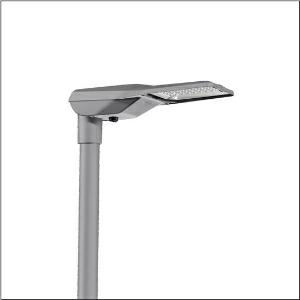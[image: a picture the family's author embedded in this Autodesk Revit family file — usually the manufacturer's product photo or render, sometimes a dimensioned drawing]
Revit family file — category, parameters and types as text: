
# Revit family: streetlight_sl_21_iq_mini___st1_0ab_5xe2m31u08jb_1fa0
name_source: partatom
category: Lighting Fixtures
units: mm (PartAtom-declared; Revit-internal decimal feet)

## family parameters
Cut with Voids When Loaded = No
Host = Face
Light Source = No
Part Type = Normal
Room Calculation Point = No
Round Connector Dimension = Use Diameter
Shared = No

## types (1)
- --- (1 x LED, 9870 lm, 72.5 W, 3000K)
    Apparent Load = 73 VA
    CIE Flux Codes = 40 74 97 100 100
    Color Rendering = 70
    Color Temperature = 3000K
    Default Elevation = 1800 mm
    Description = Streetlight SL 21 iQ mini, mast luminaire, primary light control with lens, of PMMA, primary optical cover: cover, of toughened safety glass, transparent, light distribution: ST1.0aB, light emission: direct distribution, primary light characteristic: asymmetric, installation type: post-top, side-entry, LED, High Power LED, rated luminous flux: 9.870lm, luminous efficacy: 136lm/W, light colour: 730, colour temperature: 3000K, control: presetting dimming logarithmic, Street-Remote, Auto-Match, Temp-Guard, Lumen-Switch, Night-Set, Smart-Wire, Light-Fading, Desk-Remote (wireless, voltage-free reading and setting of iQ features in the workshop via application-optimized NFC function/RFID function), optimised constant luminous flux control (CLO 2.0), mains connection: 220..240V, AC, 50/60Hz, start of lifetime: 73W, end of service life: 76W, reduction: 33W, luminaire housing, of diecast aluminium, powder-coated, Siteco® metallic grey (DB 702S), corrosivity category C5 mid according to DIN EN ISO 12944, please order mast flange separately, inclination adjustable: 0°, 5°, 10°, 15°, sealing non-destructively replaceable, multi-level sealing system, length: 628mm, width: 235mm, height: 110mm, mast flange for spigot size: 42mm (side-entry): 5XC10008XM4, 60/48mm (side-entry/post-top): 5XC10108XM2, 76/60mm (side-entry/post-top): 5XC10108XM1, Smart Interface below, protection rating (complete): IP66, insulation class (complete): insulation class II (safety insulation), certification: CE, ENEC, ENEC+, VDE, impact resistance: IK09, permissible operating ambient temperature for outdoor applications: -40..+50°C, standard-compliant lighting for roads and squares, packaging unit: 1 piece

Light Distribution: ST1.0aB
    Height = 110 mm
    Lamp = 1 x LED
    Lamp Light Flux = 9870 lm
    Lamp Power = 72.5 W
    Lamp count = 1
    Length = 625 mm
    Luminous efficacy = 136 lm/W
    Manufacturer = Siteco
    ModVariant = No
    Model = 5XE2M31U08JB
    Number of Poles = 1
    OnlyDefault = Yes
    Power Factor = 1
    Product Name = Streetlight SL 21 iQ mini | ST1.0aB
    Product group = mast luminaire | pylon top
    ProductGroupID = 6100
    Protection Class = Protection class II
    Protection Degree = IP 66
    RLX_Detail_Level = 1
    RLX_Emergency_Light_Flux = 0 lm
    RLX_Emergency_Type = 0
    RLX_Emergency_Type_DB = No
    RlxData = <blob elided: 92401 chars, md5=82f5e2b4>
    Socket = socket
    Standby Power = 0 W
    System Light Flux = 9870 lm
    System Power = 73 W
    Type Comments = factory setting: luminous flux: 100 % | dim-lin: 254 | 755 mA
    Type Image = l_1003516.jpg
    URL = http://relux.com
    VarID = @adj_042331
    Voltage = 0 V
    Weight = 0.00 kg
    Width = 234 mm

## geometry (parser evidence)
native form markers: Blend x4, Sweep x10
no freeform markers — native parametric forms only
